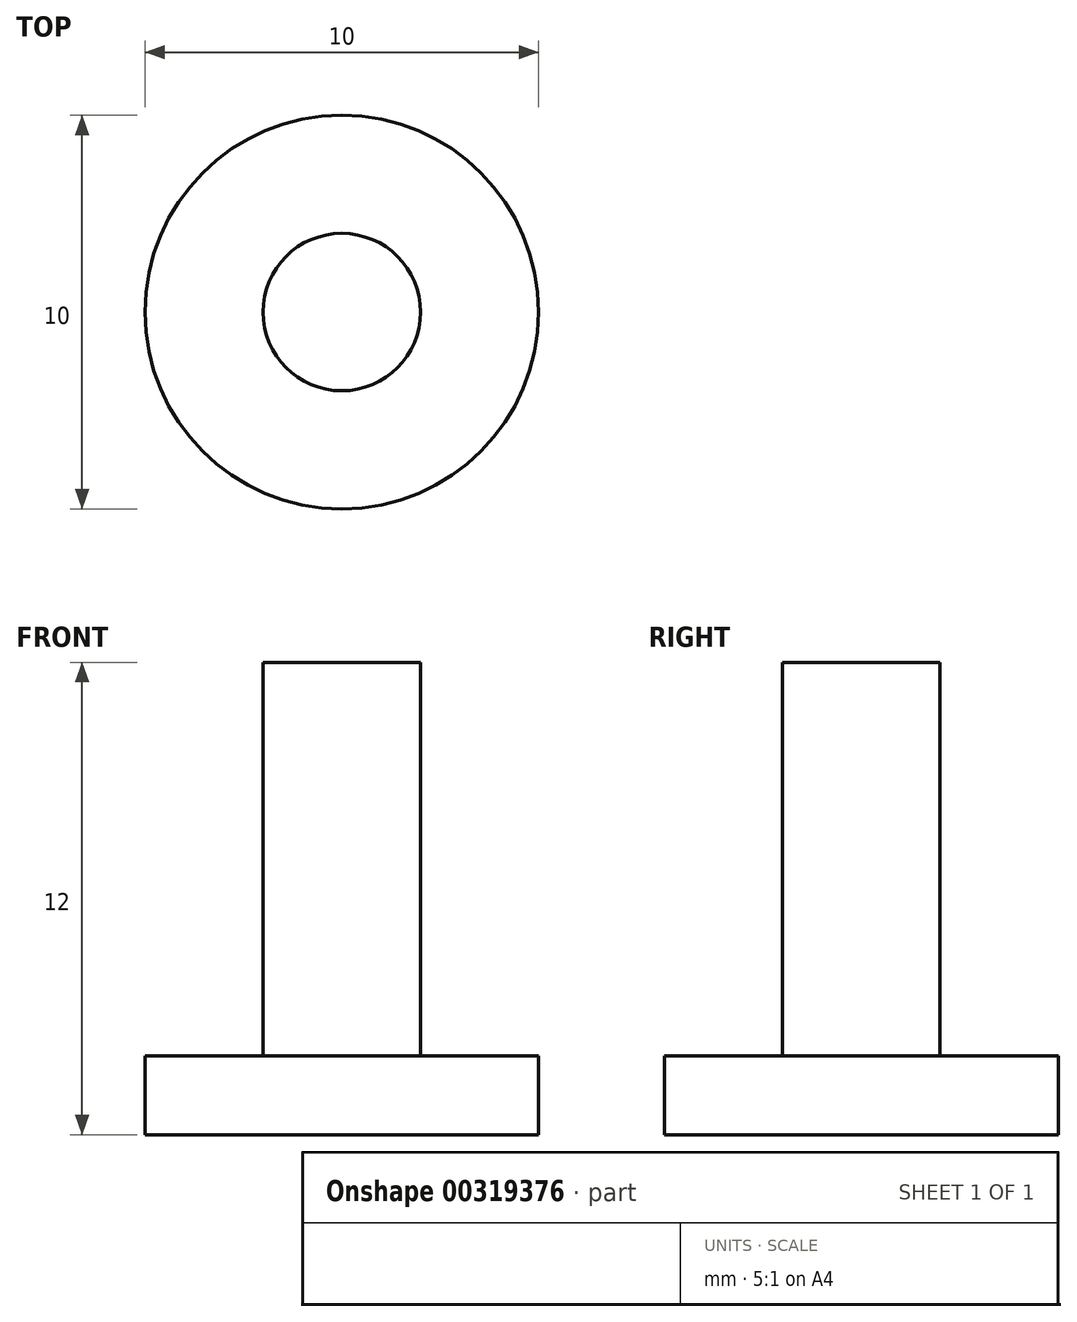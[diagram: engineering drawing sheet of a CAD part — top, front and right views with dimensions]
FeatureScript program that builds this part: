
annotation { "Feature Type Name" : "Feature", "Feature Type Description" : "" }
export const myFeature = defineFeature(function(context is Context, id is Id, definition is map)
    precondition{}
    {
        {
            var Q0;
            Q0=qCreatedBy(makeId("Top.planeOp"),FACE);
            var sketch = newSketch(context, id + "F0", { "sketchPlane" : qUnion([Q0])});
            skCircle(sketch, "E0", {"center": v(0, 0) * mm, "radius": 5 * mm});
            skSolve(sketch);
        }
        {
            var Q0;
            Q0 = qSketchRegion(id + "F0", true);
            extrude(context, id + "F1", {"entities" : qUnion([Q0]), "oppositeDirection" : true, "depth" : 2 * mm});
        }
        {
            var Q0;
            Q0=makeQuery(id+"F1.opExtrude","CAP_FACE",FACE,{"disambiguationData":[OSD([sQuery(id+"F0.wireOp",EDGE,"E0")])],"isStart":true});
            var sketch = newSketch(context, id + "F2", { "sketchPlane" : qUnion([Q0])});
            skCircle(sketch, "E1", {"center": v(0, 0) * mm, "radius": 2 * mm});
            skSolve(sketch);
        }
        {
            var Q0;
            Q0 = qSketchRegion(id + "F2", true);
            extrude(context, id + "F3", {"entities" : qUnion([Q0]), "operationType" : NewBodyOperationType.ADD, "depth" : 10 * mm});
        }
    });
